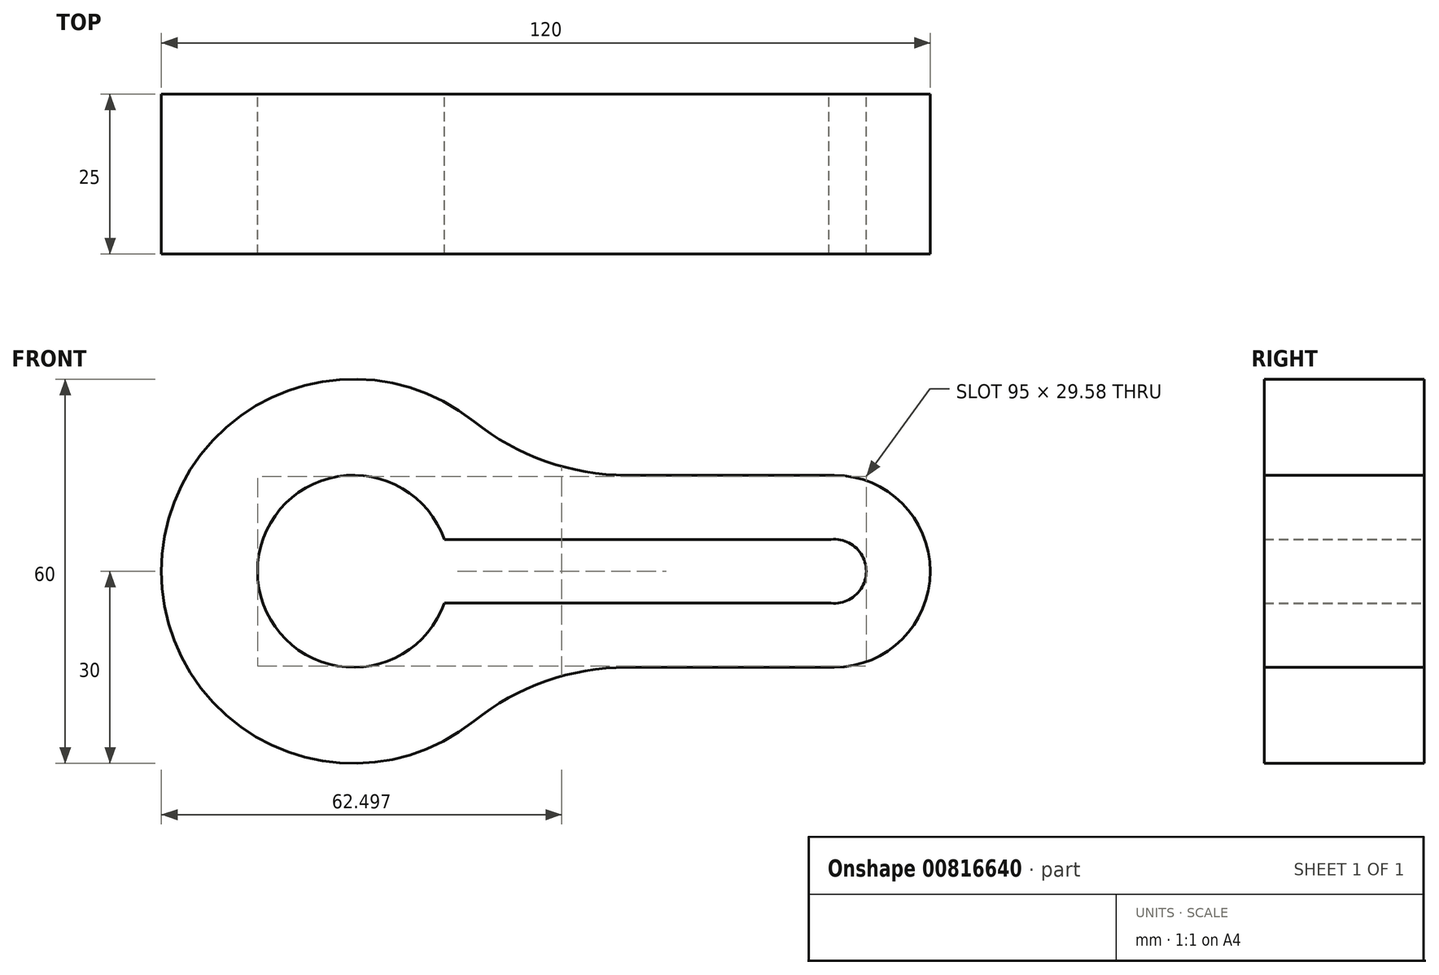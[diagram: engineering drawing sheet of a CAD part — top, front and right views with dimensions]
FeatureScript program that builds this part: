
annotation { "Feature Type Name" : "Feature", "Feature Type Description" : "" }
export const myFeature = defineFeature(function(context is Context, id is Id, definition is map)
    precondition{}
    {
        {
            var Q0;
            Q0=qCreatedBy(makeId("Front.planeOp"),FACE);
            var sketch = newSketch(context, id + "F0", { "sketchPlane" : qUnion([Q0])});
            skArc(sketch, "E0", {"start": v(-28.77, 4.93) * mm, "mid": v(-57.93, 0) * mm, "end": v(-28.77, -4.93) * mm});
            skArc(sketch, "E1", {"start": v(31.23, -4.93) * mm, "mid": v(37.07, 0) * mm, "end": v(31.23, 4.93) * mm});
            skLineSegment(sketch, "E2", {"start": v(31.23, 4.93) * mm, "end": v(-28.77, 4.93) * mm});
            skLineSegment(sketch, "E3", {"start": v(31.23, -4.93) * mm, "end": v(-28.77, -4.93) * mm});
            skArc(sketch, "E4", {"start": v(-24.14, 23.38) * mm, "mid": v(-72.93, 0) * mm, "end": v(-24.14, -23.38) * mm});
            skArc(sketch, "E5", {"start": v(32.07, -15) * mm, "mid": v(47.07, 0) * mm, "end": v(32.07, 15) * mm});
            skLineSegment(sketch, "E6", {"start": v(32.07, 15) * mm, "end": v(-0.33, 15) * mm});
            skLineSegment(sketch, "E7", {"start": v(32.07, -15) * mm, "end": v(-0.33, -15) * mm});
            skArc(sketch, "E8", {"start": v(-0.33, -15) * mm, "mid": v(-12.95, -17.16) * mm, "end": v(-24.14, -23.38) * mm});
            skArc(sketch, "E9", {"start": v(-0.33, 15) * mm, "mid": v(-12.95, 17.16) * mm, "end": v(-24.14, 23.38) * mm});
            skSolve(sketch);
        }
        {
            var Q0;
            Q0 = qSketchRegion(id + "F0", true);
            extrude(context, id + "F1", {"entities" : qUnion([Q0]), "depth" : 25 * mm, "offsetDistance" : 25 * mm});
        }
    });
